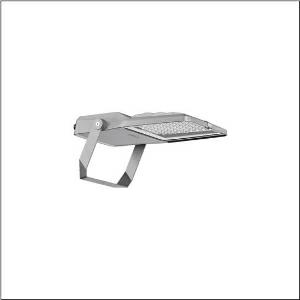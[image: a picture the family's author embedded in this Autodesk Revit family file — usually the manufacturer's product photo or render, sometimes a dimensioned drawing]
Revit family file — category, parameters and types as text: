
# Revit family: floodlight_fl_21_mini___pl43_5xa7773c4a1a_b3c2
name_source: partatom
category: Lighting Fixtures
units: mm (PartAtom-declared; Revit-internal decimal feet)

## family parameters
Cut with Voids When Loaded = No
Host = Face
Light Source = No
Part Type = Normal
Room Calculation Point = No
Round Connector Dimension = Use Diameter
Shared = No

## types (1)
- --- (1 x LED, 20890 lm, 163.5 W, 4000K)
    Apparent Load = 163 VA
    CIE Flux Codes = 27 78 99 100 100
    Color Rendering = 70
    Color Temperature = 4000K
    Default Elevation = 1800 mm
    Description = Floodlight FL 21 mini, floodlight, primary light control with lens, of PMMA, primary optical cover: protective disc, of toughened safety glass, transparent, light distribution: PL43, light emission: direct distribution, installation type: surface-mounted, LED, High Power LED, rated luminous flux: 20.890lm, luminous efficacy: 128lm/W, light colour: 740, colour temperature: 4000K, control gear: ON/OFF Multilumen, control: Temp-Guard, with terminal, 6-pole, mains connection: 220..240V, AC, 50/60Hz, start of lifetime: 164W, luminaire housing, of diecast aluminium, powder-coated, Siteco® metallic grey (DB 702S), corrosivity category C5 mid according to DIN EN ISO 12944, suitable for swimming pools, chlorine-resistant, sealing non-destructively replaceable, mounting bracket, of steel, galvanised, powder-coated, Siteco® metallic grey (DB 702S), ON/OFF, protection rating (complete): IP66, insulation class (complete): insulation class I (protective earthing), certification: CE, ENEC, VDE, protection symbol: D, impact resistance: IK08, permissible operating ambient temperature: -40..+40°C, permissible operating ambient temperature for outdoor applications: -40..+50°C, standard: DIN EN 12944, LABS conformity tested according to VDMA 24364:2018-05, packaging unit: 1 piece

Light Distribution: PL43
    Height = 70 mm
    Lamp = 1 x LED
    Lamp Light Flux = 20890 lm
    Lamp Power = 163.5 W
    Lamp count = 1
    Length = 485 mm
    Luminous efficacy = 128 lm/W
    Manufacturer = Siteco
    ModVariant = No
    Model = 5XA7773C4A1A
    Number of Poles = 1
    OnlyDefault = Yes
    Power Factor = 1
    Product Name = Floodlight FL 21 mini | PL43
    Product group = floodlight | pylon annexe
    ProductGroupID = 6200
    Protection Class = Protection class I
    Protection Degree = IP 66
    RLX_Detail_Level = 1
    RLX_Emergency_Light_Flux = 0 lm
    RLX_Emergency_Type = 0
    RLX_Emergency_Type_DB = No
    RlxData = <blob elided: 94177 chars, md5=722554b3>
    Socket = socket
    Standby Power = 0 W
    System Light Flux = 20890 lm
    System Power = 163 W
    Type Comments = factory setting: luminous flux: 100 % | (ON | - | - | - | - | - | - | -) | 825 mA
    Type Image = l_1006845.jpg
    URL = http://relux.com
    VarID = @adj_161700
    Voltage = 0 V
    Weight = 0.00 kg
    Width = 337 mm

## geometry (parser evidence)
native form markers: Blend x4, Sweep x15
no freeform markers — native parametric forms only
